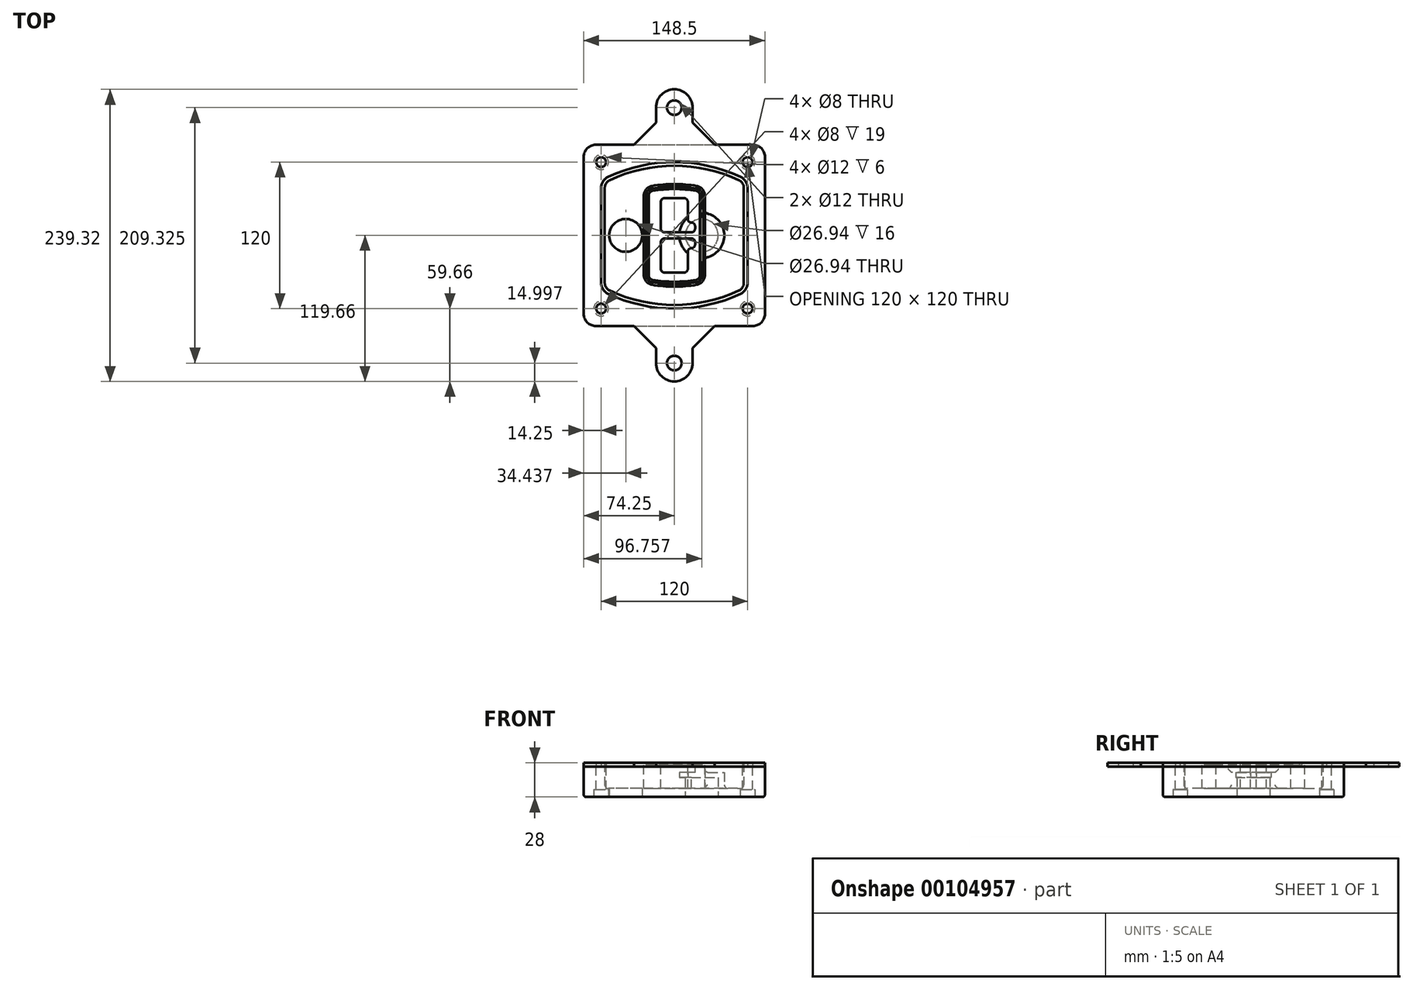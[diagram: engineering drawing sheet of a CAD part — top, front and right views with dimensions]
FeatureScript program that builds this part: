
annotation { "Feature Type Name" : "Feature", "Feature Type Description" : "" }
export const myFeature = defineFeature(function(context is Context, id is Id, definition is map)
    precondition{}
    {
        {
            var Q0;
            Q0=qCreatedBy(makeId("Top.planeOp"),FACE);
            var sketch = newSketch(context, id + "F0", { "sketchPlane" : qUnion([Q0])});
            skPoint(sketch, "E0.rect.middle", {"position": v(0, 0) * mm});
            skLineSegment(sketch, "E1.bottom", {"start": v(-64.25, -74.25) * mm, "end": v(64.25, -74.25) * mm});
            skLineSegment(sketch, "E1.top", {"start": v(-64.25, 74.25) * mm, "end": v(64.25, 74.25) * mm});
            skLineSegment(sketch, "E1.left", {"start": v(-74.25, -64.25) * mm, "end": v(-74.25, 64.25) * mm});
            skLineSegment(sketch, "E1.right", {"start": v(74.25, -64.25) * mm, "end": v(74.25, 64.25) * mm});
            skLineSegment(sketch, "E2", {"start": v(-74.25, 74.25) * mm, "end": v(74.25, -74.25) * mm, "construction": true});
            skLineSegment(sketch, "E3", {"start": v(74.25, 74.25) * mm, "end": v(-74.25, -74.25) * mm, "construction": true});
            skCircle(sketch, "E4", {"center": v(-60, 60) * mm, "radius": 4 * mm});
            skCircle(sketch, "E5", {"center": v(60, 60) * mm, "radius": 4 * mm});
            skCircle(sketch, "E6", {"center": v(60, -60) * mm, "radius": 4 * mm});
            skCircle(sketch, "E7", {"center": v(-60, -60) * mm, "radius": 4 * mm});
            skLineSegment(sketch, "E8", {"start": v(-60, 60) * mm, "end": v(60, 60) * mm, "construction": true});
            skLineSegment(sketch, "E9", {"start": v(60, 60) * mm, "end": v(60, -60) * mm, "construction": true});
            skLineSegment(sketch, "E10", {"start": v(60, -60) * mm, "end": v(-60, -60) * mm, "construction": true});
            skLineSegment(sketch, "E11", {"start": v(-60, -60) * mm, "end": v(-60, 60) * mm, "construction": true});
            skLineSegment(sketch, "E12", {"start": v(-60, 38.83) * mm, "end": v(-60, -38.83) * mm});
            skLineSegment(sketch, "E13", {"start": v(60, 38.83) * mm, "end": v(60, -38.83) * mm});
            skArc(sketch, "E14", {"start": v(54.26, 47.88) * mm, "mid": v(0, 60) * mm, "end": v(-54.26, 47.88) * mm});
            skArc(sketch, "E15", {"start": v(-54.26, -47.88) * mm, "mid": v(0, -60) * mm, "end": v(54.26, -47.88) * mm});
            skLineSegment(sketch, "E16", {"start": v(-60, 0) * mm, "end": v(60, 0) * mm, "construction": true});
            skPoint(sketch, "E17.visualSharp", {"position": v(-60, -45) * mm});
            skArc(sketch, "E17.filletArc", {"start": v(-60, -38.83) * mm, "mid": v(-58.44, -44.2) * mm, "end": v(-54.26, -47.88) * mm});
            skPoint(sketch, "E18.visualSharp", {"position": v(-60, 45) * mm});
            skArc(sketch, "E18.filletArc", {"start": v(-54.26, 47.88) * mm, "mid": v(-58.44, 44.2) * mm, "end": v(-60, 38.83) * mm});
            skPoint(sketch, "E19.visualSharp", {"position": v(60, 45) * mm});
            skArc(sketch, "E19.filletArc", {"start": v(60, 38.83) * mm, "mid": v(58.44, 44.2) * mm, "end": v(54.26, 47.88) * mm});
            skPoint(sketch, "E20.visualSharp", {"position": v(60, -45) * mm});
            skArc(sketch, "E20.filletArc", {"start": v(54.26, -47.88) * mm, "mid": v(58.44, -44.2) * mm, "end": v(60, -38.83) * mm});
            skPoint(sketch, "E21.visualSharp", {"position": v(-74.25, 74.25) * mm});
            skArc(sketch, "E21.filletArc", {"start": v(-64.25, 74.25) * mm, "mid": v(-71.32, 71.32) * mm, "end": v(-74.25, 64.25) * mm});
            skPoint(sketch, "E22.visualSharp", {"position": v(74.25, 74.25) * mm});
            skArc(sketch, "E22.filletArc", {"start": v(74.25, 64.25) * mm, "mid": v(71.32, 71.32) * mm, "end": v(64.25, 74.25) * mm});
            skPoint(sketch, "E23.visualSharp", {"position": v(74.25, -74.25) * mm});
            skArc(sketch, "E23.filletArc", {"start": v(64.25, -74.25) * mm, "mid": v(71.32, -71.32) * mm, "end": v(74.25, -64.25) * mm});
            skPoint(sketch, "E24.visualSharp", {"position": v(-74.25, -74.25) * mm});
            skArc(sketch, "E24.filletArc", {"start": v(-74.25, -64.25) * mm, "mid": v(-71.32, -71.32) * mm, "end": v(-64.25, -74.25) * mm});
            skArc(sketch, "E25.0", {"start": v(57, 38.83) * mm, "mid": v(55.9, 42.58) * mm, "end": v(52.98, 45.17) * mm});
            skLineSegment(sketch, "E25.1", {"start": v(57, 38.83) * mm, "end": v(57, -38.83) * mm});
            skArc(sketch, "E25.2", {"start": v(52.98, -45.17) * mm, "mid": v(55.9, -42.58) * mm, "end": v(57, -38.83) * mm});
            skArc(sketch, "E25.3", {"start": v(-52.98, -45.17) * mm, "mid": v(0, -57) * mm, "end": v(52.98, -45.17) * mm});
            skArc(sketch, "E25.4", {"start": v(-57, -38.83) * mm, "mid": v(-55.9, -42.58) * mm, "end": v(-52.98, -45.17) * mm});
            skArc(sketch, "E25.5", {"start": v(52.98, 45.17) * mm, "mid": v(0, 57) * mm, "end": v(-52.98, 45.17) * mm});
            skLineSegment(sketch, "E25.6", {"start": v(-57, 38.83) * mm, "end": v(-57, -38.83) * mm});
            skArc(sketch, "E25.7", {"start": v(-52.98, 45.17) * mm, "mid": v(-55.9, 42.58) * mm, "end": v(-57, 38.83) * mm});
            skArc(sketch, "E26.0", {"start": v(-55.96, 51.5) * mm, "mid": v(-61.82, 46.33) * mm, "end": v(-64, 38.83) * mm});
            skArc(sketch, "E26.1", {"start": v(55.96, 51.5) * mm, "mid": v(0, 64) * mm, "end": v(-55.96, 51.5) * mm});
            skArc(sketch, "E26.2", {"start": v(64, 38.83) * mm, "mid": v(61.82, 46.33) * mm, "end": v(55.96, 51.5) * mm});
            skLineSegment(sketch, "E26.3", {"start": v(64, 38.83) * mm, "end": v(64, -38.83) * mm});
            skArc(sketch, "E26.4", {"start": v(55.96, -51.5) * mm, "mid": v(61.82, -46.33) * mm, "end": v(64, -38.83) * mm});
            skLineSegment(sketch, "E26.5", {"start": v(-64, 38.83) * mm, "end": v(-64, -38.83) * mm});
            skArc(sketch, "E26.6", {"start": v(-55.96, -51.5) * mm, "mid": v(0, -64) * mm, "end": v(55.96, -51.5) * mm});
            skArc(sketch, "E26.7", {"start": v(-64, -38.83) * mm, "mid": v(-61.82, -46.33) * mm, "end": v(-55.96, -51.5) * mm});
            skSolve(sketch);
        }
        {
            var Q0;
            Q0=makeQuery(id+"F0.imprint","IMPRINT",FACE,{"disambiguationData":[TD([[makeQuery(id+"F0.imprint","IMPRINT",EDGE,{"derivedFrom":sQuery(id+"F0.wireOp",EDGE,"E1.bottom")}),1.0]])]});
            var Q1;
            Q1=makeQuery(id+"F0.imprint","IMPRINT",FACE,{"disambiguationData":[TD([[makeQuery(id+"F0.imprint","IMPRINT",EDGE,{"derivedFrom":sQuery(id+"F0.wireOp",EDGE,"E12")}),1.0]])]});
            var Q2;
            Q2=makeQuery(id+"F0.imprint","IMPRINT",FACE,{"disambiguationData":[TD([[makeQuery(id+"F0.imprint","IMPRINT",EDGE,{"derivedFrom":sQuery(id+"F0.wireOp",EDGE,"E25.0")}),1.0]])]});
            var Q3;
            Q3=makeQuery(id+"F0.imprint","IMPRINT",FACE,{"disambiguationData":[TD([[makeQuery(id+"F0.imprint","IMPRINT",EDGE,{"derivedFrom":sQuery(id+"F0.wireOp",EDGE,"E12")}),-1.0]])]});
            extrude(context, id + "F1", {"entities" : qUnion([Q0, Q1, Q2, Q3]), "oppositeDirection" : true, "depth" : 25 * mm});
        }
        {
            var Q0;
            Q0=makeQuery(id+"F0.imprint","IMPRINT",FACE,{"disambiguationData":[TD([[makeQuery(id+"F0.imprint","IMPRINT",EDGE,{"derivedFrom":sQuery(id+"F0.wireOp",EDGE,"E12")}),1.0]])]});
            extrude(context, id + "F2", {"entities" : qUnion([Q0]), "operationType" : NewBodyOperationType.ADD, "depth" : 3 * mm});
        }
        {
            var Q0;
            Q0=makeQuery(id+"F0.imprint","IMPRINT",FACE,{"disambiguationData":[TD([[makeQuery(id+"F0.imprint","IMPRINT",EDGE,{"derivedFrom":sQuery(id+"F0.wireOp",EDGE,"E25.0")}),1.0]])]});
            extrude(context, id + "F3", {"entities" : qUnion([Q0]), "operationType" : NewBodyOperationType.REMOVE, "oppositeDirection" : true, "depth" : 18 * mm});
        }
        {
            var Q0;
            Q0=makeQuery(id+"F2.opExtrude","CAP_FACE",FACE,{"disambiguationData":[OSD([sQuery(id+"F0.wireOp",EDGE,"E12"),sQuery(id+"F0.wireOp",EDGE,"E13"),sQuery(id+"F0.wireOp",EDGE,"E14"),sQuery(id+"F0.wireOp",EDGE,"E15"),sQuery(id+"F0.wireOp",EDGE,"E17.filletArc"),sQuery(id+"F0.wireOp",EDGE,"E18.filletArc"),sQuery(id+"F0.wireOp",EDGE,"E19.filletArc"),sQuery(id+"F0.wireOp",EDGE,"E20.filletArc"),sQuery(id+"F0.wireOp",EDGE,"E25.0"),sQuery(id+"F0.wireOp",EDGE,"E25.1"),sQuery(id+"F0.wireOp",EDGE,"E25.2"),sQuery(id+"F0.wireOp",EDGE,"E25.3"),sQuery(id+"F0.wireOp",EDGE,"E25.4"),sQuery(id+"F0.wireOp",EDGE,"E25.5"),sQuery(id+"F0.wireOp",EDGE,"E25.6"),sQuery(id+"F0.wireOp",EDGE,"E25.7")])],"isStart":false});
            var sketch = newSketch(context, id + "F4", { "sketchPlane" : qUnion([Q0])});
            skArc(sketch, "E27.0", {"start": v(-18.34, -40.45) * mm, "mid": v(0, -42) * mm, "end": v(18.34, -40.45) * mm});
            skArc(sketch, "E28.0", {"start": v(18.34, 40.45) * mm, "mid": v(0, 42) * mm, "end": v(-18.34, 40.45) * mm});
            skLineSegment(sketch, "E29", {"start": v(-25, 32.57) * mm, "end": v(-25, -32.57) * mm});
            skLineSegment(sketch, "E30", {"start": v(25, 32.57) * mm, "end": v(25, -32.57) * mm});
            skLineSegment(sketch, "E31", {"start": v(-25, 39.1) * mm, "end": v(25, 39.1) * mm, "construction": true});
            skLineSegment(sketch, "E32", {"start": v(-25, -39.1) * mm, "end": v(25, -39.1) * mm, "construction": true});
            skPoint(sketch, "E33.visualSharp", {"position": v(-25, 39.1) * mm});
            skArc(sketch, "E33.filletArc", {"start": v(-18.34, 40.45) * mm, "mid": v(-23.11, 37.73) * mm, "end": v(-25, 32.57) * mm});
            skPoint(sketch, "E34.visualSharp", {"position": v(25, 39.1) * mm});
            skArc(sketch, "E34.filletArc", {"start": v(25, 32.57) * mm, "mid": v(23.11, 37.73) * mm, "end": v(18.34, 40.45) * mm});
            skPoint(sketch, "E35.visualSharp", {"position": v(25, -39.1) * mm});
            skArc(sketch, "E35.filletArc", {"start": v(18.34, -40.45) * mm, "mid": v(23.11, -37.73) * mm, "end": v(25, -32.57) * mm});
            skPoint(sketch, "E36.visualSharp", {"position": v(-25, -39.1) * mm});
            skArc(sketch, "E36.filletArc", {"start": v(-25, -32.57) * mm, "mid": v(-23.11, -37.73) * mm, "end": v(-18.34, -40.45) * mm});
            skArc(sketch, "E37.0", {"start": v(52.98, 45.17) * mm, "mid": v(0, 57) * mm, "end": v(-52.98, 45.17) * mm});
            skArc(sketch, "E37.1", {"start": v(-52.98, 45.17) * mm, "mid": v(-55.9, 42.58) * mm, "end": v(-57, 38.83) * mm});
            skLineSegment(sketch, "E37.2", {"start": v(-57, 38.83) * mm, "end": v(-57, -38.83) * mm});
            skArc(sketch, "E37.3", {"start": v(-57, -38.83) * mm, "mid": v(-55.9, -42.58) * mm, "end": v(-52.98, -45.17) * mm});
            skArc(sketch, "E37.4", {"start": v(-52.98, -45.17) * mm, "mid": v(0, -57) * mm, "end": v(52.98, -45.17) * mm});
            skArc(sketch, "E37.5", {"start": v(52.98, -45.17) * mm, "mid": v(55.9, -42.58) * mm, "end": v(57, -38.83) * mm});
            skLineSegment(sketch, "E37.6", {"start": v(57, 38.83) * mm, "end": v(57, -38.83) * mm});
            skArc(sketch, "E37.7", {"start": v(57, 38.83) * mm, "mid": v(55.9, 42.58) * mm, "end": v(52.98, 45.17) * mm});
            skLineSegment(sketch, "E38.0", {"start": v(23, 32.57) * mm, "end": v(23, -32.57) * mm});
            skArc(sketch, "E38.1", {"start": v(18, -38.48) * mm, "mid": v(21.58, -36.44) * mm, "end": v(23, -32.57) * mm});
            skArc(sketch, "E38.2", {"start": v(-18, -38.48) * mm, "mid": v(0, -40) * mm, "end": v(18, -38.48) * mm});
            skArc(sketch, "E38.3", {"start": v(-23, -32.57) * mm, "mid": v(-21.58, -36.44) * mm, "end": v(-18, -38.48) * mm});
            skLineSegment(sketch, "E38.4", {"start": v(-23, 32.57) * mm, "end": v(-23, -32.57) * mm});
            skArc(sketch, "E38.5", {"start": v(23, 32.57) * mm, "mid": v(21.58, 36.44) * mm, "end": v(18, 38.48) * mm});
            skArc(sketch, "E38.6", {"start": v(-18, 38.48) * mm, "mid": v(-21.58, 36.44) * mm, "end": v(-23, 32.57) * mm});
            skArc(sketch, "E38.7", {"start": v(18, 38.48) * mm, "mid": v(0, 40) * mm, "end": v(-18, 38.48) * mm});
            skArc(sketch, "E39.0", {"start": v(21, 32.57) * mm, "mid": v(20.06, 35.15) * mm, "end": v(17.67, 36.5) * mm});
            skLineSegment(sketch, "E39.1", {"start": v(21, 32.57) * mm, "end": v(21, -32.57) * mm});
            skArc(sketch, "E39.2", {"start": v(17.67, -36.5) * mm, "mid": v(20.06, -35.15) * mm, "end": v(21, -32.57) * mm});
            skArc(sketch, "E39.3", {"start": v(-17.67, -36.5) * mm, "mid": v(0, -38) * mm, "end": v(17.67, -36.5) * mm});
            skArc(sketch, "E39.4", {"start": v(-21, -32.57) * mm, "mid": v(-20.06, -35.15) * mm, "end": v(-17.67, -36.5) * mm});
            skArc(sketch, "E39.5", {"start": v(17.67, 36.5) * mm, "mid": v(0, 38) * mm, "end": v(-17.67, 36.5) * mm});
            skLineSegment(sketch, "E39.6", {"start": v(-21, 32.57) * mm, "end": v(-21, -32.57) * mm});
            skArc(sketch, "E39.7", {"start": v(-17.67, 36.5) * mm, "mid": v(-20.06, 35.15) * mm, "end": v(-21, 32.57) * mm});
            skLineSegment(sketch, "E40", {"start": v(-25, 0) * mm, "end": v(25, 0) * mm, "construction": true});
            skLineSegment(sketch, "E41", {"start": v(-11, 5.5) * mm, "end": v(-11, 27.5) * mm});
            skLineSegment(sketch, "E42", {"start": v(-8, 30.5) * mm, "end": v(8, 30.5) * mm});
            skLineSegment(sketch, "E43", {"start": v(11, 27.5) * mm, "end": v(11, 13.5) * mm});
            skLineSegment(sketch, "E44", {"start": v(14, 10.5) * mm, "end": v(14, 10.5) * mm});
            skLineSegment(sketch, "E45", {"start": v(17, 7.5) * mm, "end": v(17, 5.5) * mm});
            skLineSegment(sketch, "E46", {"start": v(14, 2.5) * mm, "end": v(-8, 2.5) * mm});
            skPoint(sketch, "E47.visualSharp", {"position": v(-11, 30.5) * mm});
            skArc(sketch, "E47.filletArc", {"start": v(-8, 30.5) * mm, "mid": v(-10.12, 29.62) * mm, "end": v(-11, 27.5) * mm});
            skPoint(sketch, "E48.visualSharp", {"position": v(11, 30.5) * mm});
            skArc(sketch, "E48.filletArc", {"start": v(11, 27.5) * mm, "mid": v(10.12, 29.62) * mm, "end": v(8, 30.5) * mm});
            skPoint(sketch, "E49.visualSharp", {"position": v(11, 10.5) * mm});
            skArc(sketch, "E49.filletArc", {"start": v(11, 13.5) * mm, "mid": v(11.88, 11.38) * mm, "end": v(14, 10.5) * mm});
            skPoint(sketch, "E50.visualSharp", {"position": v(17, 10.5) * mm});
            skArc(sketch, "E50.filletArc", {"start": v(17, 7.5) * mm, "mid": v(16.12, 9.62) * mm, "end": v(14, 10.5) * mm});
            skPoint(sketch, "E51.visualSharp", {"position": v(17, 2.5) * mm});
            skArc(sketch, "E51.filletArc", {"start": v(14, 2.5) * mm, "mid": v(16.12, 3.38) * mm, "end": v(17, 5.5) * mm});
            skPoint(sketch, "E52.visualSharp", {"position": v(-11, 2.5) * mm});
            skArc(sketch, "E52.filletArc", {"start": v(-11, 5.5) * mm, "mid": v(-10.12, 3.38) * mm, "end": v(-8, 2.5) * mm});
            skLineSegment(sketch, "E53.0.MirrorCS", {"start": v(14, -2.5) * mm, "end": v(-8, -2.5) * mm});
            skArc(sketch, "E54.0.MirrorCS", {"start": v(-11, -5.5) * mm, "mid": v(-10.12, -3.38) * mm, "end": v(-8, -2.5) * mm});
            skLineSegment(sketch, "E55.0.MirrorCS", {"start": v(-11, -5.5) * mm, "end": v(-11, -27.5) * mm});
            skArc(sketch, "E56.0.MirrorCS", {"start": v(-8, -30.5) * mm, "mid": v(-10.12, -29.62) * mm, "end": v(-11, -27.5) * mm});
            skLineSegment(sketch, "E57.0.MirrorCS", {"start": v(-8, -30.5) * mm, "end": v(8, -30.5) * mm});
            skArc(sketch, "E58.0.MirrorCS", {"start": v(11, -27.5) * mm, "mid": v(10.12, -29.62) * mm, "end": v(8, -30.5) * mm});
            skLineSegment(sketch, "E59.0.MirrorCS", {"start": v(11, -27.5) * mm, "end": v(11, -13.5) * mm});
            skArc(sketch, "E60.0.MirrorCS", {"start": v(11, -13.5) * mm, "mid": v(11.88, -11.38) * mm, "end": v(14, -10.5) * mm});
            skArc(sketch, "E61.0.MirrorCS", {"start": v(17, -7.5) * mm, "mid": v(16.12, -9.62) * mm, "end": v(14, -10.5) * mm});
            skLineSegment(sketch, "E62.0.MirrorCS", {"start": v(17, -7.5) * mm, "end": v(17, -5.5) * mm});
            skArc(sketch, "E63.0.MirrorCS", {"start": v(14, -2.5) * mm, "mid": v(16.12, -3.38) * mm, "end": v(17, -5.5) * mm});
            skSolve(sketch);
        }
        {
            var Q0;
            Q0=makeQuery(id+"F4.imprint","IMPRINT",FACE,{"disambiguationData":[TD([[makeQuery(id+"F4.imprint","IMPRINT",EDGE,{"derivedFrom":sQuery(id+"F4.wireOp",EDGE,"E27.0")}),1.0]])]});
            var Q1;
            Q1=makeQuery(id+"F4.imprint","IMPRINT",FACE,{"disambiguationData":[TD([[makeQuery(id+"F4.imprint","IMPRINT",EDGE,{"derivedFrom":sQuery(id+"F4.wireOp",EDGE,"E38.0")}),-1.0]])]});
            var Q2;
            Q2=makeQuery(id+"F4.imprint","IMPRINT",FACE,{"disambiguationData":[TD([[makeQuery(id+"F4.imprint","IMPRINT",EDGE,{"derivedFrom":sQuery(id+"F4.wireOp",EDGE,"E39.0")}),1.0]])]});
            extrude(context, id + "F5", {"entities" : qUnion([Q0, Q1, Q2]), "operationType" : NewBodyOperationType.ADD, "endBound" : BoundingType.UP_TO_NEXT, "oppositeDirection" : true, "depth" : 25 * mm});
        }
        {
            var Q0;
            Q0=makeQuery(id+"F4.imprint","IMPRINT",FACE,{"disambiguationData":[TD([[makeQuery(id+"F4.imprint","IMPRINT",EDGE,{"derivedFrom":sQuery(id+"F4.wireOp",EDGE,"E38.0")}),-1.0]])]});
            extrude(context, id + "F6", {"entities" : qUnion([Q0]), "operationType" : NewBodyOperationType.REMOVE, "oppositeDirection" : true, "depth" : 2 * mm});
        }
        {
            var Q0;
            Q0=makeQuery(id+"F1.opExtrude","CAP_FACE",FACE,{"disambiguationData":[OSD([sQuery(id+"F0.wireOp",EDGE,"E1.bottom"),sQuery(id+"F0.wireOp",EDGE,"E1.top"),sQuery(id+"F0.wireOp",EDGE,"E1.left"),sQuery(id+"F0.wireOp",EDGE,"E1.right"),sQuery(id+"F0.wireOp",EDGE,"E4"),sQuery(id+"F0.wireOp",EDGE,"E5"),sQuery(id+"F0.wireOp",EDGE,"E6"),sQuery(id+"F0.wireOp",EDGE,"E7"),sQuery(id+"F0.wireOp",EDGE,"E21.filletArc"),sQuery(id+"F0.wireOp",EDGE,"E22.filletArc"),sQuery(id+"F0.wireOp",EDGE,"E23.filletArc"),sQuery(id+"F0.wireOp",EDGE,"E24.filletArc")])],"isStart":false});
            var sketch = newSketch(context, id + "F7", { "sketchPlane" : qUnion([Q0])});
            skCircle(sketch, "E64", {"center": v(22.5, 0) * mm, "radius": 13.47 * mm});
            skCircle(sketch, "E65", {"center": v(-39.81, 0) * mm, "radius": 13.47 * mm});
            skLineSegment(sketch, "E66", {"start": v(74.25, 0) * mm, "end": v(-74.25, 0) * mm});
            skCircle(sketch, "E67", {"center": v(22.5, 0) * mm, "radius": 18.47 * mm});
            skCircle(sketch, "E68", {"center": v(60, -60) * mm, "radius": 6 * mm});
            skCircle(sketch, "E69", {"center": v(-60, -60) * mm, "radius": 6 * mm});
            skCircle(sketch, "E70", {"center": v(-60, 60) * mm, "radius": 6 * mm});
            skCircle(sketch, "E71", {"center": v(60, 60) * mm, "radius": 6 * mm});
            skSolve(sketch);
        }
        {
            var Q0;
            {var subQ1=sQuery(id+"F7.wireOp",EDGE,"E66");var subQ4=sQuery(id+"F7.wireOp",EDGE,"E64");var subQ6=makeQuery(id+"F7.imprint","INTERSECT",VERTEX,{"disambiguationData":[OD(0.0)],"derivedFrom":[subQ4,subQ1]});Q0=makeQuery(id+"F7.imprint","IMPRINT",FACE,{"disambiguationData":[TD([[makeQuery(id+"F7.imprint","IMPRINT",EDGE,{"disambiguationData":[TD([[subQ6,-1.0]])],"derivedFrom":subQ4}),-1.0]])]});}
            var Q1;
            {var subQ0=sQuery(id+"F7.wireOp",EDGE,"E66");var subQ1=sQuery(id+"F7.wireOp",EDGE,"E64");var subQ3=makeQuery(id+"F7.imprint","INTERSECT",VERTEX,{"disambiguationData":[OD(0.0)],"derivedFrom":[subQ1,subQ0]});Q1=makeQuery(id+"F7.imprint","IMPRINT",FACE,{"disambiguationData":[TD([[makeQuery(id+"F7.imprint","IMPRINT",EDGE,{"disambiguationData":[TD([[subQ3,-1.0]])],"derivedFrom":subQ1}),1.0]])]});}
            var Q2;
            {var subQ0=sQuery(id+"F7.wireOp",EDGE,"E66");var subQ1=sQuery(id+"F7.wireOp",EDGE,"E64");var subQ3=makeQuery(id+"F7.imprint","INTERSECT",VERTEX,{"disambiguationData":[OD(0.0)],"derivedFrom":[subQ1,subQ0]});Q2=makeQuery(id+"F7.imprint","IMPRINT",FACE,{"disambiguationData":[TD([[makeQuery(id+"F7.imprint","IMPRINT",EDGE,{"disambiguationData":[TD([[subQ3,1.0]])],"derivedFrom":subQ1}),1.0]])]});}
            var Q3;
            {var subQ1=sQuery(id+"F7.wireOp",EDGE,"E66");var subQ4=sQuery(id+"F7.wireOp",EDGE,"E64");var subQ6=makeQuery(id+"F7.imprint","INTERSECT",VERTEX,{"disambiguationData":[OD(0.0)],"derivedFrom":[subQ4,subQ1]});Q3=makeQuery(id+"F7.imprint","IMPRINT",FACE,{"disambiguationData":[TD([[makeQuery(id+"F7.imprint","IMPRINT",EDGE,{"disambiguationData":[TD([[subQ6,1.0]])],"derivedFrom":subQ4}),-1.0]])]});}
            extrude(context, id + "F8", {"entities" : qUnion([Q0, Q1, Q2, Q3]), "operationType" : NewBodyOperationType.ADD, "oppositeDirection" : true, "depth" : 20 * mm});
        }
        {
            var Q0;
            {var subQ0=sQuery(id+"F7.wireOp",EDGE,"E66");var subQ1=sQuery(id+"F7.wireOp",EDGE,"E64");var subQ3=makeQuery(id+"F7.imprint","INTERSECT",VERTEX,{"disambiguationData":[OD(0.0)],"derivedFrom":[subQ1,subQ0]});Q0=makeQuery(id+"F7.imprint","IMPRINT",FACE,{"disambiguationData":[TD([[makeQuery(id+"F7.imprint","IMPRINT",EDGE,{"disambiguationData":[TD([[subQ3,-1.0]])],"derivedFrom":subQ1}),1.0]])]});}
            var Q1;
            {var subQ0=sQuery(id+"F7.wireOp",EDGE,"E66");var subQ1=sQuery(id+"F7.wireOp",EDGE,"E64");var subQ3=makeQuery(id+"F7.imprint","INTERSECT",VERTEX,{"disambiguationData":[OD(0.0)],"derivedFrom":[subQ1,subQ0]});Q1=makeQuery(id+"F7.imprint","IMPRINT",FACE,{"disambiguationData":[TD([[makeQuery(id+"F7.imprint","IMPRINT",EDGE,{"disambiguationData":[TD([[subQ3,1.0]])],"derivedFrom":subQ1}),1.0]])]});}
            extrude(context, id + "F9", {"entities" : qUnion([Q0, Q1]), "operationType" : NewBodyOperationType.REMOVE, "oppositeDirection" : true, "depth" : 16 * mm});
        }
        {
            var Q0;
            {var subQ0=sQuery(id+"F7.wireOp",EDGE,"E66");var subQ1=sQuery(id+"F7.wireOp",EDGE,"E65");var subQ3=makeQuery(id+"F7.imprint","INTERSECT",VERTEX,{"disambiguationData":[OD(0.0)],"derivedFrom":[subQ1,subQ0]});Q0=makeQuery(id+"F7.imprint","IMPRINT",FACE,{"disambiguationData":[TD([[makeQuery(id+"F7.imprint","IMPRINT",EDGE,{"disambiguationData":[TD([[subQ3,-1.0]])],"derivedFrom":subQ1}),1.0]])]});}
            var Q1;
            {var subQ0=sQuery(id+"F7.wireOp",EDGE,"E66");var subQ1=sQuery(id+"F7.wireOp",EDGE,"E65");var subQ3=makeQuery(id+"F7.imprint","INTERSECT",VERTEX,{"disambiguationData":[OD(0.0)],"derivedFrom":[subQ1,subQ0]});Q1=makeQuery(id+"F7.imprint","IMPRINT",FACE,{"disambiguationData":[TD([[makeQuery(id+"F7.imprint","IMPRINT",EDGE,{"disambiguationData":[TD([[subQ3,1.0]])],"derivedFrom":subQ1}),1.0]])]});}
            extrude(context, id + "F10", {"entities" : qUnion([Q0, Q1]), "operationType" : NewBodyOperationType.REMOVE, "oppositeDirection" : true, "depth" : 25 * mm});
        }
        {
            var Q0;
            Q0=makeQuery(id+"F7.imprint","IMPRINT",FACE,{"disambiguationData":[TD([[makeQuery(id+"F7.imprint","IMPRINT",EDGE,{"derivedFrom":sQuery(id+"F7.wireOp",EDGE,"E68")}),1.0]])]});
            var Q1;
            Q1=makeQuery(id+"F7.imprint","IMPRINT",FACE,{"disambiguationData":[TD([[makeQuery(id+"F7.imprint","IMPRINT",EDGE,{"derivedFrom":makeQuery(id+"F1.opExtrude","CAP_EDGE",EDGE,{"disambiguationData":[OSD([sQuery(id+"F0.wireOp",EDGE,"E5")])],"isStart":false})}),-1.0]])]});
            var Q2;
            Q2=makeQuery(id+"F7.imprint","IMPRINT",FACE,{"disambiguationData":[TD([[makeQuery(id+"F7.imprint","IMPRINT",EDGE,{"derivedFrom":sQuery(id+"F7.wireOp",EDGE,"E69")}),1.0]])]});
            var Q3;
            Q3=makeQuery(id+"F7.imprint","IMPRINT",FACE,{"disambiguationData":[TD([[makeQuery(id+"F7.imprint","IMPRINT",EDGE,{"derivedFrom":makeQuery(id+"F1.opExtrude","CAP_EDGE",EDGE,{"disambiguationData":[OSD([sQuery(id+"F0.wireOp",EDGE,"E4")])],"isStart":false})}),-1.0]])]});
            var Q4;
            Q4=makeQuery(id+"F7.imprint","IMPRINT",FACE,{"disambiguationData":[TD([[makeQuery(id+"F7.imprint","IMPRINT",EDGE,{"derivedFrom":sQuery(id+"F7.wireOp",EDGE,"E70")}),1.0]])]});
            var Q5;
            Q5=makeQuery(id+"F7.imprint","IMPRINT",FACE,{"disambiguationData":[TD([[makeQuery(id+"F7.imprint","IMPRINT",EDGE,{"derivedFrom":makeQuery(id+"F1.opExtrude","CAP_EDGE",EDGE,{"disambiguationData":[OSD([sQuery(id+"F0.wireOp",EDGE,"E7")])],"isStart":false})}),-1.0]])]});
            var Q6;
            Q6=makeQuery(id+"F7.imprint","IMPRINT",FACE,{"disambiguationData":[TD([[makeQuery(id+"F7.imprint","IMPRINT",EDGE,{"derivedFrom":sQuery(id+"F7.wireOp",EDGE,"E71")}),1.0]])]});
            var Q7;
            Q7=makeQuery(id+"F7.imprint","IMPRINT",FACE,{"disambiguationData":[TD([[makeQuery(id+"F7.imprint","IMPRINT",EDGE,{"derivedFrom":makeQuery(id+"F1.opExtrude","CAP_EDGE",EDGE,{"disambiguationData":[OSD([sQuery(id+"F0.wireOp",EDGE,"E6")])],"isStart":false})}),-1.0]])]});
            extrude(context, id + "F11", {"entities" : qUnion([Q0, Q1, Q2, Q3, Q4, Q5, Q6, Q7]), "operationType" : NewBodyOperationType.REMOVE, "oppositeDirection" : true, "depth" : 6 * mm});
        }
        {
            var Q0;
            Q0=makeQuery(id+"F9.boolean.opBoolean","COPY",FACE,{"derivedFrom":makeQuery(id+"F9.opExtrude","CAP_FACE",FACE,{"disambiguationData":[OSD([sQuery(id+"F7.wireOp",EDGE,"E64")])],"isStart":false})});
            var sketch = newSketch(context, id + "F12", { "sketchPlane" : qUnion([Q0])});
            skArc(sketch, "E72.0", {"start": v(11, 14.45) * mm, "mid": v(6.45, 9.13) * mm, "end": v(4.2, 2.5) * mm});
            skArc(sketch, "E72.1", {"start": v(4.2, -2.5) * mm, "mid": v(6.45, -9.13) * mm, "end": v(11, -14.45) * mm});
            skLineSegment(sketch, "E73", {"start": v(4.2, -2.5) * mm, "end": v(14, -2.5) * mm});
            skLineSegment(sketch, "E74.0", {"start": v(14, 2.5) * mm, "end": v(4.2, 2.5) * mm});
            skArc(sketch, "E74.1", {"start": v(14, 2.5) * mm, "mid": v(16.12, 3.38) * mm, "end": v(17, 5.5) * mm});
            skLineSegment(sketch, "E74.2", {"start": v(17, 7.5) * mm, "end": v(17, 5.5) * mm});
            skArc(sketch, "E74.3", {"start": v(17, 7.5) * mm, "mid": v(16.12, 9.62) * mm, "end": v(14, 10.5) * mm});
            skArc(sketch, "E74.4", {"start": v(11, 13.5) * mm, "mid": v(11.88, 11.38) * mm, "end": v(14, 10.5) * mm});
            skLineSegment(sketch, "E74.5", {"start": v(11, 14.45) * mm, "end": v(11, 13.5) * mm});
            skLineSegment(sketch, "E74.7", {"start": v(14, -2.5) * mm, "end": v(4.2, -2.5) * mm});
            skArc(sketch, "E74.8", {"start": v(14, -2.5) * mm, "mid": v(16.12, -3.38) * mm, "end": v(17, -5.5) * mm});
            skLineSegment(sketch, "E74.9", {"start": v(17, -7.5) * mm, "end": v(17, -5.5) * mm});
            skArc(sketch, "E74.10", {"start": v(17, -7.5) * mm, "mid": v(16.12, -9.62) * mm, "end": v(14, -10.5) * mm});
            skArc(sketch, "E74.11", {"start": v(11, -13.5) * mm, "mid": v(11.88, -11.38) * mm, "end": v(14, -10.5) * mm});
            skLineSegment(sketch, "E74.12", {"start": v(11, -14.45) * mm, "end": v(11, -13.5) * mm});
            skPoint(sketch, "E75.orphan", {"position": v(11, -27.5) * mm});
            skPoint(sketch, "E76.orphan", {"position": v(-8, -2.5) * mm});
            skPoint(sketch, "E77.orphan", {"position": v(-8, 2.5) * mm});
            skPoint(sketch, "E78.orphan", {"position": v(11, 27.5) * mm});
            skSolve(sketch);
        }
        {
            var Q0;
            {var subQ7=sQuery(id+"F12.wireOp",EDGE,"E72.0");var subQ14=sQuery(id+"F12.wireOp",EDGE,"E72.1");var subQ16=sQuery(id+"F12.wireOp",EDGE,"E74.1");var subQ18=sQuery(id+"F12.wireOp",EDGE,"E74.8");Q0=qUnion([makeQuery(id+"F12.imprint","IMPRINT",FACE,{"disambiguationData":[TD([[makeQuery(id+"F12.imprint","IMPRINT",EDGE,{"derivedFrom":subQ7}),1.0]])]}),makeQuery(id+"F12.imprint","IMPRINT",FACE,{"disambiguationData":[TD([[makeQuery(id+"F12.imprint","IMPRINT",EDGE,{"derivedFrom":subQ14}),1.0]])]}),makeQuery(id+"F12.imprint","IMPRINT",FACE,{"disambiguationData":[TD([[makeQuery(id+"F12.imprint","IMPRINT",EDGE,{"derivedFrom":subQ16}),1.0]])]}),makeQuery(id+"F12.imprint","IMPRINT",FACE,{"disambiguationData":[TD([[makeQuery(id+"F12.imprint","IMPRINT",EDGE,{"derivedFrom":subQ18}),-1.0]])]})]);}
            var Q1;
            Q1=makeQuery(id+"F5.boolean.opBoolean","SPLIT",FACE,{"disambiguationData":[TD([makeQuery(id+"F5.opExtrude","SWEPT_FACE",FACE,{"disambiguationData":[OSD([sQuery(id+"F4.wireOp",EDGE,"E41")])]})])],"derivedFrom":makeQuery(id+"F3.boolean.opBoolean","COPY",FACE,{"derivedFrom":makeQuery(id+"F3.opExtrude","CAP_FACE",FACE,{"disambiguationData":[OSD([sQuery(id+"F0.wireOp",EDGE,"E25.0"),sQuery(id+"F0.wireOp",EDGE,"E25.1"),sQuery(id+"F0.wireOp",EDGE,"E25.2"),sQuery(id+"F0.wireOp",EDGE,"E25.3"),sQuery(id+"F0.wireOp",EDGE,"E25.4"),sQuery(id+"F0.wireOp",EDGE,"E25.5"),sQuery(id+"F0.wireOp",EDGE,"E25.6"),sQuery(id+"F0.wireOp",EDGE,"E25.7")])],"isStart":false})})});
            extrude(context, id + "F13", {"entities" : qUnion([Q0]), "operationType" : NewBodyOperationType.REMOVE, "endBound" : BoundingType.UP_TO_SURFACE, "endBoundEntityFace" : qUnion([Q1]), "depth" : 25 * mm});
        }
        {
            var Q0;
            Q0=makeQuery(id+"F3.boolean.opBoolean","COPY",EDGE,{"derivedFrom":makeQuery(id+"F3.opExtrude","CAP_EDGE",EDGE,{"disambiguationData":[OSD([sQuery(id+"F0.wireOp",EDGE,"E25.6")])],"isStart":false})});
            var Q1;
            Q1=makeQuery(id+"F8.boolean.opBoolean","INTERSECT",EDGE,{"derivedFrom":[makeQuery(id+"F5.opExtrude","SWEPT_FACE",FACE,{"disambiguationData":[OSD([sQuery(id+"F4.wireOp",EDGE,"E30")])]}),makeQuery(id+"F8.opExtrude","CAP_FACE",FACE,{"disambiguationData":[OSD([sQuery(id+"F7.wireOp",EDGE,"E67")])],"isStart":false})]});
            var Q2;
            Q2=makeQuery(id+"F8.boolean.opBoolean","INTERSECT",EDGE,{"disambiguationData":[OD(1.0)],"derivedFrom":[makeQuery(id+"F5.opExtrude","SWEPT_FACE",FACE,{"disambiguationData":[OSD([sQuery(id+"F4.wireOp",EDGE,"E30")])]}),makeQuery(id+"F8.opExtrude","SWEPT_FACE",FACE,{"disambiguationData":[OSD([sQuery(id+"F7.wireOp",EDGE,"E67")])]})]});
            var Q3;
            {var subQ0=makeQuery(id+"F3.boolean.opBoolean","COPY",FACE,{"derivedFrom":makeQuery(id+"F3.opExtrude","CAP_FACE",FACE,{"disambiguationData":[OSD([sQuery(id+"F0.wireOp",EDGE,"E25.0"),sQuery(id+"F0.wireOp",EDGE,"E25.1"),sQuery(id+"F0.wireOp",EDGE,"E25.2"),sQuery(id+"F0.wireOp",EDGE,"E25.3"),sQuery(id+"F0.wireOp",EDGE,"E25.4"),sQuery(id+"F0.wireOp",EDGE,"E25.5"),sQuery(id+"F0.wireOp",EDGE,"E25.6"),sQuery(id+"F0.wireOp",EDGE,"E25.7")])],"isStart":false})});var subQ1=sQuery(id+"F4.wireOp",EDGE,"E30");Q3=makeQuery(id+"F8.boolean.opBoolean","SPLIT",EDGE,{"disambiguationData":[TD([makeQuery(id+"F5.opExtrude","SWEPT_FACE",FACE,{"disambiguationData":[OSD([sQuery(id+"F4.wireOp",EDGE,"E35.filletArc")])]})])],"derivedFrom":makeQuery(id+"F5.opExtrude","TWEAK_EDGE",EDGE,{"derivedFrom":[subQ0,makeQuery(id+"F4.imprint","IMPRINT",EDGE,{"derivedFrom":subQ1})]})});}
            var Q4;
            {var subQ0=sQuery(id+"F0.wireOp",EDGE,"E25.0");var subQ1=sQuery(id+"F0.wireOp",EDGE,"E25.1");var subQ2=sQuery(id+"F0.wireOp",EDGE,"E25.2");var subQ3=sQuery(id+"F0.wireOp",EDGE,"E25.3");var subQ4=sQuery(id+"F0.wireOp",EDGE,"E25.4");var subQ5=sQuery(id+"F0.wireOp",EDGE,"E25.5");var subQ6=sQuery(id+"F0.wireOp",EDGE,"E25.6");var subQ7=sQuery(id+"F0.wireOp",EDGE,"E25.7");Q4=makeQuery(id+"F8.boolean.opBoolean","INTERSECT",EDGE,{"derivedFrom":[makeQuery(id+"F5.boolean.opBoolean","SPLIT",FACE,{"disambiguationData":[TD([makeQuery(id+"F2.opExtrude","SWEPT_FACE",FACE,{"disambiguationData":[OSD([subQ0])]})])],"derivedFrom":makeQuery(id+"F3.boolean.opBoolean","COPY",FACE,{"derivedFrom":makeQuery(id+"F3.opExtrude","CAP_FACE",FACE,{"disambiguationData":[OSD([subQ0,subQ1,subQ2,subQ3,subQ4,subQ5,subQ6,subQ7])],"isStart":false})})}),makeQuery(id+"F8.opExtrude","SWEPT_FACE",FACE,{"disambiguationData":[OSD([sQuery(id+"F7.wireOp",EDGE,"E67")])]})]});}
            var Q5;
            Q5=makeQuery(id+"F8.boolean.opBoolean","INTERSECT",EDGE,{"disambiguationData":[OD(0.0)],"derivedFrom":[makeQuery(id+"F5.opExtrude","SWEPT_FACE",FACE,{"disambiguationData":[OSD([sQuery(id+"F4.wireOp",EDGE,"E30")])]}),makeQuery(id+"F8.opExtrude","SWEPT_FACE",FACE,{"disambiguationData":[OSD([sQuery(id+"F7.wireOp",EDGE,"E67")])]})]});
            fillet(context, id + "F14", {"entities" : qUnion([Q0, Q1, Q2, Q3, Q4, Q5]), "radius" : 3 * mm, "tangentPropagation" : true, "allowEdgeOverflow" : false});
        }
        {
            var Q0;
            Q0=makeQuery(id+"F1.opExtrude","CAP_EDGE",EDGE,{"disambiguationData":[OSD([sQuery(id+"F0.wireOp",EDGE,"E1.bottom")])],"isStart":false});
            fillet(context, id + "F15", {"entities" : qUnion([Q0]), "radius" : 2 * mm, "tangentPropagation" : true, "allowEdgeOverflow" : false});
        }
        {
            var Q0;
            {var subQ0=sQuery(id+"F0.wireOp",EDGE,"E22.filletArc");var subQ1=sQuery(id+"F0.wireOp",EDGE,"E7");var subQ2=sQuery(id+"F0.wireOp",EDGE,"E6");var subQ3=sQuery(id+"F0.wireOp",EDGE,"E5");var subQ4=sQuery(id+"F0.wireOp",EDGE,"E4");var subQ5=sQuery(id+"F0.wireOp",EDGE,"E1.bottom");var subQ6=sQuery(id+"F0.wireOp",EDGE,"E21.filletArc");var subQ7=sQuery(id+"F0.wireOp",EDGE,"E1.top");var subQ8=sQuery(id+"F0.wireOp",EDGE,"E1.left");var subQ9=sQuery(id+"F0.wireOp",EDGE,"E1.right");var subQ10=sQuery(id+"F0.wireOp",EDGE,"E23.filletArc");var subQ11=sQuery(id+"F0.wireOp",EDGE,"E24.filletArc");Q0=makeQuery(id+"F2.boolean.opBoolean","SPLIT",FACE,{"disambiguationData":[TD([makeQuery(id+"F1.opExtrude","SWEPT_FACE",FACE,{"disambiguationData":[OSD([subQ5])]})])],"derivedFrom":makeQuery(id+"F1.opExtrude","CAP_FACE",FACE,{"disambiguationData":[OSD([subQ5,subQ7,subQ8,subQ9,subQ4,subQ3,subQ2,subQ1,subQ6,subQ0,subQ10,subQ11])],"isStart":true})});}
            var sketch = newSketch(context, id + "F16", { "sketchPlane" : qUnion([Q0])});
            skLineSegment(sketch, "E79", {"start": v(0, 74.25) * mm, "end": v(0, 104.66) * mm, "construction": true});
            skLineSegment(sketch, "E80", {"start": v(-33, 74.25) * mm, "end": v(-15, 92.25) * mm});
            skLineSegment(sketch, "E81", {"start": v(33, 74.25) * mm, "end": v(15, 92.25) * mm});
            skLineSegment(sketch, "E82", {"start": v(15, 92.25) * mm, "end": v(15, 104.66) * mm});
            skLineSegment(sketch, "E83", {"start": v(-15, 92.25) * mm, "end": v(-15, 104.66) * mm});
            skArc(sketch, "E84", {"start": v(15, 104.66) * mm, "mid": v(0, 119.66) * mm, "end": v(-15, 104.66) * mm});
            skCircle(sketch, "E85", {"center": v(0, 104.66) * mm, "radius": 6 * mm});
            skLineSegment(sketch, "E86", {"start": v(-74.25, 0) * mm, "end": v(74.25, 0) * mm, "construction": true});
            skLineSegment(sketch, "E87.MirrorCS", {"start": v(33, -74.25) * mm, "end": v(15, -92.25) * mm});
            skLineSegment(sketch, "E88.MirrorCS", {"start": v(15, -92.25) * mm, "end": v(15, -104.66) * mm});
            skArc(sketch, "E89.MirrorCS", {"start": v(15, -104.66) * mm, "mid": v(0, -119.66) * mm, "end": v(-15, -104.66) * mm});
            skLineSegment(sketch, "E90.MirrorCS", {"start": v(-15, -92.25) * mm, "end": v(-15, -104.66) * mm});
            skLineSegment(sketch, "E91.MirrorCS", {"start": v(-33, -74.25) * mm, "end": v(-15, -92.25) * mm});
            skCircle(sketch, "E92.MirrorC", {"center": v(0, -104.66) * mm, "radius": 6 * mm});
            skSolve(sketch);
        }
        {
            var Q0;
            Q0=makeQuery(id+"F16.imprint","IMPRINT",FACE,{"disambiguationData":[TD([[makeQuery(id+"F16.imprint","IMPRINT",EDGE,{"derivedFrom":makeQuery(id+"F1.opExtrude","CAP_EDGE",EDGE,{"disambiguationData":[OSD([sQuery(id+"F0.wireOp",EDGE,"E1.left")])],"isStart":true})}),-1.0]])]});
            var Q1;
            {var subQ0=sQuery(id+"F16.wireOp",EDGE,"E80");Q1=makeQuery(id+"F16.imprint","IMPRINT",FACE,{"disambiguationData":[TD([[makeQuery(id+"F16.imprint","IMPRINT",EDGE,{"derivedFrom":subQ0}),-1.0]])]});}
            var Q2;
            {var subQ0=sQuery(id+"F16.wireOp",EDGE,"E87.MirrorCS");Q2=makeQuery(id+"F16.imprint","IMPRINT",FACE,{"disambiguationData":[TD([[makeQuery(id+"F16.imprint","IMPRINT",EDGE,{"derivedFrom":subQ0}),-1.0]])]});}
            var Q3;
            Q3=makeQuery(id+"F2.opExtrude","CAP_FACE",FACE,{"disambiguationData":[OSD([sQuery(id+"F0.wireOp",EDGE,"E12"),sQuery(id+"F0.wireOp",EDGE,"E13"),sQuery(id+"F0.wireOp",EDGE,"E14"),sQuery(id+"F0.wireOp",EDGE,"E15"),sQuery(id+"F0.wireOp",EDGE,"E17.filletArc"),sQuery(id+"F0.wireOp",EDGE,"E18.filletArc"),sQuery(id+"F0.wireOp",EDGE,"E19.filletArc"),sQuery(id+"F0.wireOp",EDGE,"E20.filletArc"),sQuery(id+"F0.wireOp",EDGE,"E25.0"),sQuery(id+"F0.wireOp",EDGE,"E25.1"),sQuery(id+"F0.wireOp",EDGE,"E25.2"),sQuery(id+"F0.wireOp",EDGE,"E25.3"),sQuery(id+"F0.wireOp",EDGE,"E25.4"),sQuery(id+"F0.wireOp",EDGE,"E25.5"),sQuery(id+"F0.wireOp",EDGE,"E25.6"),sQuery(id+"F0.wireOp",EDGE,"E25.7")])],"isStart":false});
            extrude(context, id + "F17", {"entities" : qUnion([Q0, Q1, Q2]), "endBound" : BoundingType.UP_TO_SURFACE, "endBoundEntityFace" : qUnion([Q3]), "depth" : 25 * mm});
        }
    });
